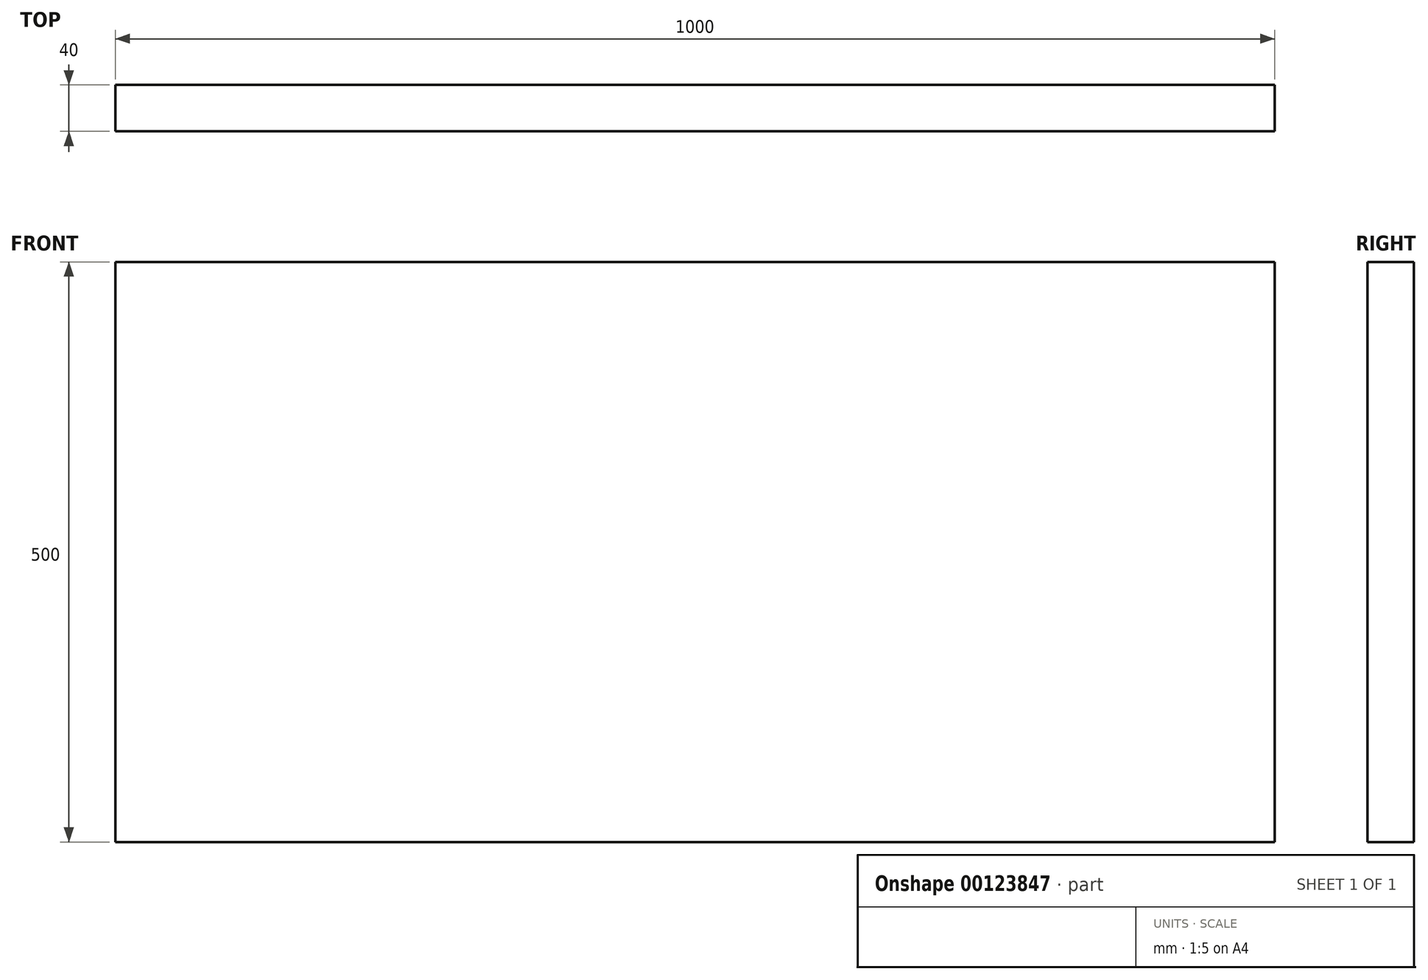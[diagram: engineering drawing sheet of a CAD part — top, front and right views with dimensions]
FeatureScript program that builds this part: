
annotation { "Feature Type Name" : "Feature", "Feature Type Description" : "" }
export const myFeature = defineFeature(function(context is Context, id is Id, definition is map)
    precondition{}
    {
        {
            var Q0;
            Q0=qCreatedBy(makeId("Front.planeOp"),FACE);
            var sketch = newSketch(context, id + "F0", { "sketchPlane" : qUnion([Q0])});
            skLineSegment(sketch, "E0.bottom", {"start": v(-1024.57, 100.26) * mm, "end": v(-24.57, 100.26) * mm});
            skLineSegment(sketch, "E0.top", {"start": v(-1024.57, -399.74) * mm, "end": v(-24.57, -399.74) * mm});
            skLineSegment(sketch, "E0.left", {"start": v(-1024.57, 100.26) * mm, "end": v(-1024.57, -399.74) * mm});
            skLineSegment(sketch, "E0.right", {"start": v(-24.57, 100.26) * mm, "end": v(-24.57, -399.74) * mm});
            skSolve(sketch);
        }
        {
            var Q0;
            Q0=makeQuery(id+"F0.imprint","IMPRINT",FACE,{"disambiguationData":[TD([[makeQuery(id+"F0.imprint","IMPRINT",EDGE,{"derivedFrom":sQuery(id+"F0.wireOp",EDGE,"E0.bottom")}),-1.0]])]});
            extrude(context, id + "F1", {"entities" : qUnion([Q0]), "depth" : 40 * mm});
        }
    });
